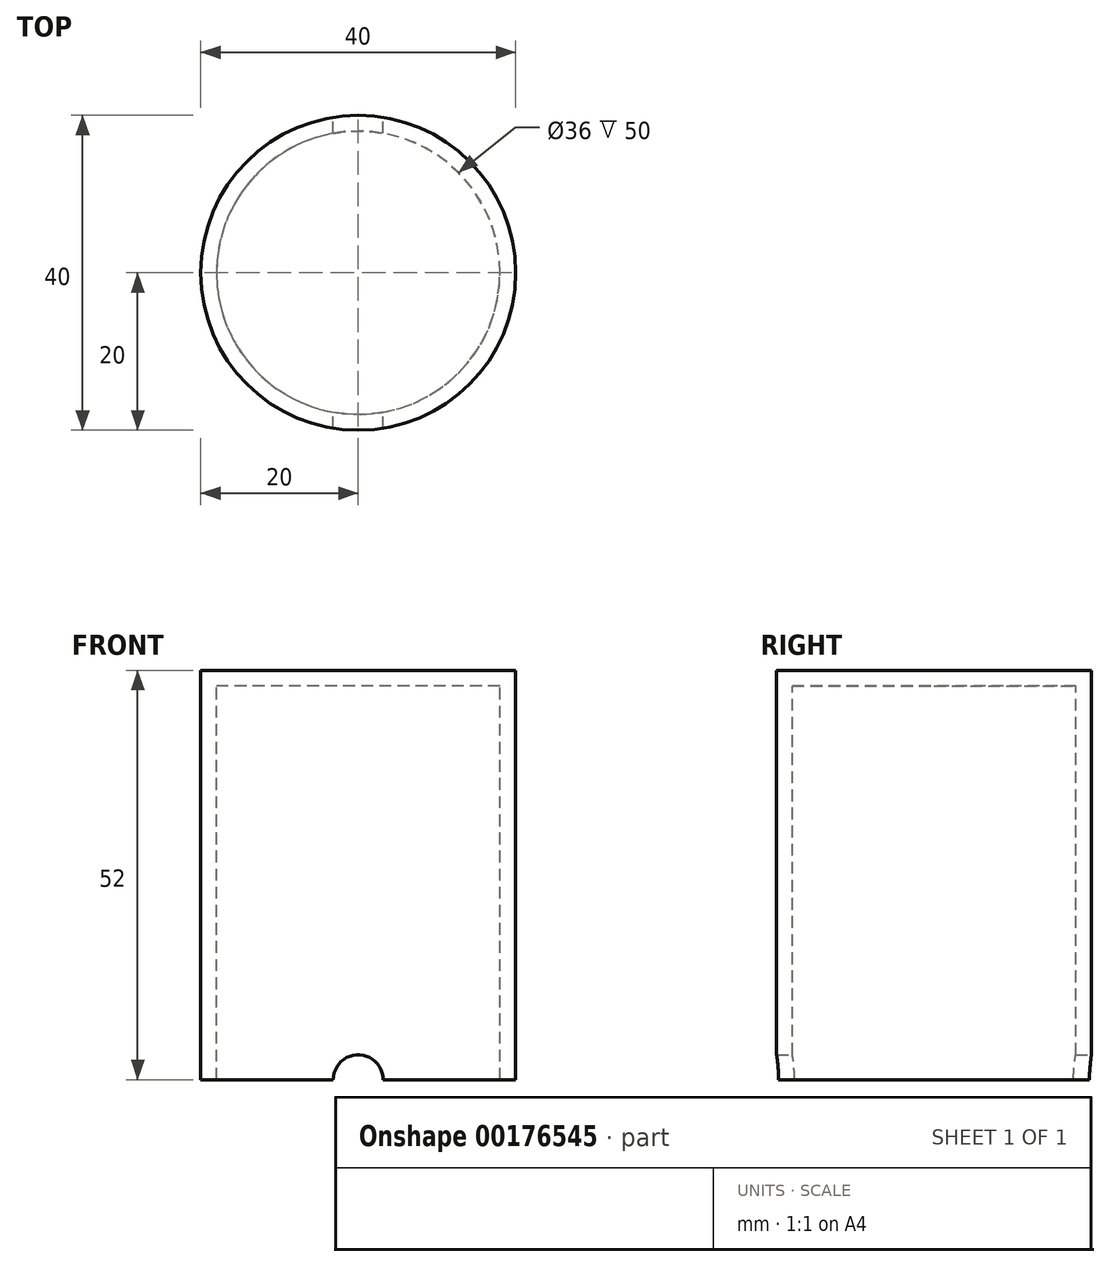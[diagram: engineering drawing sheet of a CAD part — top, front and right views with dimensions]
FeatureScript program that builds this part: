
annotation { "Feature Type Name" : "Feature", "Feature Type Description" : "" }
export const myFeature = defineFeature(function(context is Context, id is Id, definition is map)
    precondition{}
    {
        {
            var Q0;
            Q0=qCreatedBy(makeId("Front.planeOp"),FACE);
            var sketch = newSketch(context, id + "F0", { "sketchPlane" : qUnion([Q0])});
            skLineSegment(sketch, "E0.bottom", {"start": v(-18, 0) * mm, "end": v(18, 0) * mm});
            skLineSegment(sketch, "E0.top", {"start": v(-18, 50) * mm, "end": v(18, 50) * mm});
            skLineSegment(sketch, "E0.left", {"start": v(-18, 0) * mm, "end": v(-18, 50) * mm});
            skLineSegment(sketch, "E0.right", {"start": v(18, 0) * mm, "end": v(18, 50) * mm});
            skLineSegment(sketch, "E1.top", {"start": v(18, 50) * mm, "end": v(-18, 50) * mm});
            skLineSegment(sketch, "E1.right", {"start": v(-18, 52) * mm, "end": v(-18, 50) * mm});
            skLineSegment(sketch, "E2.bottom", {"start": v(-18, 52) * mm, "end": v(-20, 52) * mm});
            skLineSegment(sketch, "E2.top", {"start": v(-18, 0) * mm, "end": v(-20, 0) * mm});
            skLineSegment(sketch, "E2.left", {"start": v(-18, 52) * mm, "end": v(-18, 0) * mm});
            skLineSegment(sketch, "E2.right", {"start": v(-20, 52) * mm, "end": v(-20, 0) * mm});
            skLineSegment(sketch, "E3", {"start": v(0, 52) * mm, "end": v(0, 50) * mm});
            skLineSegment(sketch, "E4.bottom", {"start": v(-18, 52) * mm, "end": v(0, 52) * mm});
            skLineSegment(sketch, "E4.top", {"start": v(-18, 50) * mm, "end": v(0, 50) * mm});
            skSolve(sketch);
        }
        {
            var Q0;
            Q0=makeQuery(id+"F0.imprint","IMPRINT",FACE,{"disambiguationData":[TD([[makeQuery(id+"F0.imprint","IMPRINT",EDGE,{"derivedFrom":sQuery(id+"F0.wireOp",EDGE,"E4.bottom")}),-1.0]])]});
            var Q1;
            Q1=makeQuery(id+"F0.imprint","IMPRINT",FACE,{"disambiguationData":[TD([[makeQuery(id+"F0.imprint","IMPRINT",EDGE,{"derivedFrom":sQuery(id+"F0.wireOp",EDGE,"E2.bottom")}),1.0]])]});
            var Q2;
            Q2=sQuery(id+"F0.wireOp",EDGE,"E3");
            revolve(context, id + "F1", {"entities" : qUnion([Q0, Q1]), "axis" : qUnion([Q2]), "revolveType" : RevolveType.FULL});
        }
        {
            var Q0;
            Q0=qCreatedBy(makeId("Front.planeOp"),FACE);
            var sketch = newSketch(context, id + "F2", { "sketchPlane" : qUnion([Q0])});
            skCircle(sketch, "E5", {"center": v(0, 0) * mm, "radius": 3.18 * mm});
            skSolve(sketch);
        }
        {
            var Q0;
            Q0=makeQuery(id+"F2.imprint","IMPRINT",FACE,{"disambiguationData":[TD([[makeQuery(id+"F2.imprint","IMPRINT",EDGE,{"derivedFrom":sQuery(id+"F2.wireOp",EDGE,"E5")}),1.0]])]});
            extrude(context, id + "F3", {"entities" : qUnion([Q0]), "operationType" : NewBodyOperationType.REMOVE, "endBound" : BoundingType.THROUGH_ALL, "depth" : 25.4 * mm, "hasSecondDirection" : true, "secondDirectionBound" : SecondDirectionBoundingType.THROUGH_ALL, "secondDirectionOppositeDirection" : true, "secondDirectionDepth" : 25.4 * mm});
        }
    });
